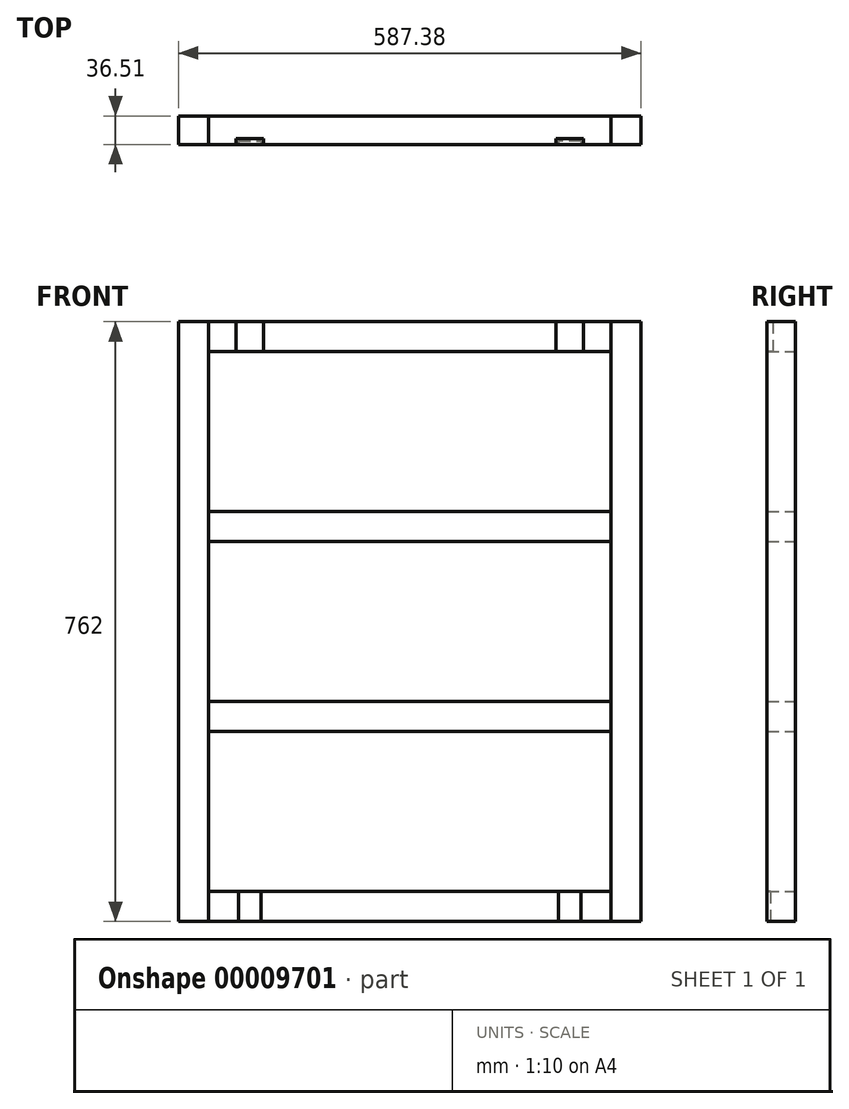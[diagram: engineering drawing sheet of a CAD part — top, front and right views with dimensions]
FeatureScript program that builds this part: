
annotation { "Feature Type Name" : "Feature", "Feature Type Description" : "" }
export const myFeature = defineFeature(function(context is Context, id is Id, definition is map)
    precondition{}
    {
        {
            var Q0;
            Q0=qCreatedBy(makeId("Front.planeOp"),FACE);
            var sketch = newSketch(context, id + "F0", { "sketchPlane" : qUnion([Q0])});
            skLineSegment(sketch, "E0.rect.bottom", {"start": v(293.69, 381) * mm, "end": v(-293.69, 381) * mm});
            skLineSegment(sketch, "E0.rect.top", {"start": v(293.69, -381) * mm, "end": v(-293.69, -381) * mm});
            skLineSegment(sketch, "E0.rect.left", {"start": v(293.69, 381) * mm, "end": v(293.69, -381) * mm});
            skLineSegment(sketch, "E0.rect.right", {"start": v(-293.69, 381) * mm, "end": v(-293.69, -381) * mm});
            skPoint(sketch, "E0.rect.middle", {"position": v(0, 0) * mm});
            skLineSegment(sketch, "E1.0", {"start": v(255.59, 342.9) * mm, "end": v(-255.59, 342.9) * mm});
            skLineSegment(sketch, "E1.1", {"start": v(255.59, 342.9) * mm, "end": v(255.59, -342.9) * mm});
            skLineSegment(sketch, "E1.2", {"start": v(255.59, -342.9) * mm, "end": v(-255.59, -342.9) * mm});
            skLineSegment(sketch, "E1.3", {"start": v(-255.59, 342.9) * mm, "end": v(-255.59, -342.9) * mm});
            skLineSegment(sketch, "E2", {"start": v(-255.59, 342.9) * mm, "end": v(-255.59, 381) * mm});
            skLineSegment(sketch, "E3", {"start": v(255.59, 342.9) * mm, "end": v(255.59, 381) * mm});
            skLineSegment(sketch, "E4", {"start": v(-255.59, -342.9) * mm, "end": v(-255.59, -381) * mm});
            skLineSegment(sketch, "E5", {"start": v(255.59, -342.9) * mm, "end": v(255.59, -381) * mm});
            skLineSegment(sketch, "E6", {"start": v(-255.59, 139.7) * mm, "end": v(255.59, 139.7) * mm});
            skLineSegment(sketch, "E7", {"start": v(-255.59, 101.6) * mm, "end": v(255.59, 101.6) * mm});
            skLineSegment(sketch, "E8", {"start": v(-255.59, -101.6) * mm, "end": v(255.59, -101.6) * mm});
            skLineSegment(sketch, "E9", {"start": v(-255.59, -139.7) * mm, "end": v(255.59, -139.7) * mm});
            skLineSegment(sketch, "E10", {"start": v(0, 342.9) * mm, "end": v(0, 139.7) * mm, "construction": true});
            skLineSegment(sketch, "E11", {"start": v(0, 101.6) * mm, "end": v(0, -101.6) * mm, "construction": true});
            skLineSegment(sketch, "E12", {"start": v(0, -139.7) * mm, "end": v(0, -342.9) * mm, "construction": true});
            skLineSegment(sketch, "E13", {"start": v(0, 139.7) * mm, "end": v(0, 101.6) * mm, "construction": true});
            skLineSegment(sketch, "E14", {"start": v(0, -101.6) * mm, "end": v(0, -139.7) * mm, "construction": true});
            skSolve(sketch);
        }
        {
            var Q0;
            {var subQ7=sQuery(id+"F0.wireOp",EDGE,"E0.rect.right");Q0=makeQuery(id+"F0.imprint","IMPRINT",FACE,{"disambiguationData":[TD([[makeQuery(id+"F0.imprint","IMPRINT",EDGE,{"derivedFrom":subQ7}),1.0]])]});}
            var Q1;
            {var subQ7=sQuery(id+"F0.wireOp",EDGE,"E0.rect.left");Q1=makeQuery(id+"F0.imprint","IMPRINT",FACE,{"disambiguationData":[TD([[makeQuery(id+"F0.imprint","IMPRINT",EDGE,{"derivedFrom":subQ7}),-1.0]])]});}
            extrude(context, id + "F1", {"entities" : qUnion([Q0, Q1]), "depth" : 36.5 * mm});
        }
        {
            var Q0;
            Q0=makeQuery(id+"F0.imprint","IMPRINT",FACE,{"disambiguationData":[TD([[makeQuery(id+"F0.imprint","IMPRINT",EDGE,{"derivedFrom":sQuery(id+"F0.wireOp",EDGE,"E1.0")}),-1.0]])]});
            var Q1;
            {var subQ1=sQuery(id+"F0.wireOp",EDGE,"E6");Q1=makeQuery(id+"F0.imprint","IMPRINT",FACE,{"disambiguationData":[TD([[makeQuery(id+"F0.imprint","IMPRINT",EDGE,{"derivedFrom":subQ1}),-1.0]])]});}
            var Q2;
            {var subQ0=sQuery(id+"F0.wireOp",EDGE,"E8");Q2=makeQuery(id+"F0.imprint","IMPRINT",FACE,{"disambiguationData":[TD([[makeQuery(id+"F0.imprint","IMPRINT",EDGE,{"derivedFrom":subQ0}),-1.0]])]});}
            var Q3;
            Q3=makeQuery(id+"F0.imprint","IMPRINT",FACE,{"disambiguationData":[TD([[makeQuery(id+"F0.imprint","IMPRINT",EDGE,{"derivedFrom":sQuery(id+"F0.wireOp",EDGE,"E1.2")}),1.0]])]});
            var Q4;
            Q4=makeQuery(id+"F1.opExtrude","CAP_FACE",FACE,{"disambiguationData":[OSD([sQuery(id+"F0.wireOp",EDGE,"E0.rect.bottom"),sQuery(id+"F0.wireOp",EDGE,"E0.rect.top"),sQuery(id+"F0.wireOp",EDGE,"E0.rect.right"),sQuery(id+"F0.wireOp",EDGE,"E1.3"),sQuery(id+"F0.wireOp",EDGE,"E2"),sQuery(id+"F0.wireOp",EDGE,"E4")])],"isStart":false});
            extrude(context, id + "F2", {"entities" : qUnion([Q0, Q1, Q2, Q3]), "endBound" : BoundingType.UP_TO_SURFACE, "endBoundEntityFace" : qUnion([Q4]), "depth" : 25.4 * mm});
        }
        {
            var Q0;
            {var subQ0=sQuery(id+"F0.wireOp",EDGE,"E2");var subQ1=sQuery(id+"F0.wireOp",EDGE,"E0.rect.bottom");Q0=makeQuery(id+"F2.opExtrude","CAP_FACE",FACE,{"disambiguationData":[OSD([subQ1,sQuery(id+"F0.wireOp",EDGE,"E0.rect.top"),sQuery(id+"F0.wireOp",EDGE,"E0.rect.right"),sQuery(id+"F0.wireOp",EDGE,"E1.3"),subQ0,sQuery(id+"F0.wireOp",EDGE,"E4")]),ownerDisambiguation([makeQuery(id+"F2.opExtrude","SWEPT_BODY",BODY,{"disambiguationData":[OSD([subQ1,sQuery(id+"F0.wireOp",EDGE,"E1.0"),subQ0,sQuery(id+"F0.wireOp",EDGE,"E3")])]})])],"isStart":false});}
            var sketch = newSketch(context, id + "F3", { "sketchPlane" : qUnion([Q0])});
            skLineSegment(sketch, "E15.bottom", {"start": v(-220.66, 381) * mm, "end": v(-185.74, 381) * mm});
            skLineSegment(sketch, "E15.top", {"start": v(-220.66, 342.9) * mm, "end": v(-185.74, 342.9) * mm});
            skLineSegment(sketch, "E15.left", {"start": v(-220.66, 381) * mm, "end": v(-220.66, 342.9) * mm});
            skLineSegment(sketch, "E15.right", {"start": v(-185.74, 381) * mm, "end": v(-185.74, 342.9) * mm});
            skLineSegment(sketch, "E16.bottom", {"start": v(-217.49, -342.9) * mm, "end": v(-188.91, -342.9) * mm});
            skLineSegment(sketch, "E16.top", {"start": v(-217.49, -381) * mm, "end": v(-188.91, -381) * mm});
            skLineSegment(sketch, "E16.left", {"start": v(-217.49, -342.9) * mm, "end": v(-217.49, -381) * mm});
            skLineSegment(sketch, "E16.right", {"start": v(-188.91, -342.9) * mm, "end": v(-188.91, -381) * mm});
            skLineSegment(sketch, "E17", {"start": v(-203.2, 342.9) * mm, "end": v(-203.2, -342.9) * mm, "construction": true});
            skLineSegment(sketch, "E18", {"start": v(0, 342.9) * mm, "end": v(0, -342.9) * mm, "construction": true});
            skLineSegment(sketch, "E19.MirrorCS", {"start": v(185.74, 381) * mm, "end": v(185.74, 342.9) * mm});
            skLineSegment(sketch, "E20.MirrorCS", {"start": v(220.66, 381) * mm, "end": v(220.66, 342.9) * mm});
            skLineSegment(sketch, "E21.MirrorCS", {"start": v(220.66, 342.9) * mm, "end": v(185.74, 342.9) * mm});
            skLineSegment(sketch, "E22.MirrorCS", {"start": v(220.66, 381) * mm, "end": v(185.74, 381) * mm});
            skLineSegment(sketch, "E23.MirrorCS", {"start": v(217.49, -342.9) * mm, "end": v(188.91, -342.9) * mm});
            skLineSegment(sketch, "E24.MirrorCS", {"start": v(188.91, -342.9) * mm, "end": v(188.91, -381) * mm});
            skLineSegment(sketch, "E25.MirrorCS", {"start": v(217.49, -381) * mm, "end": v(188.91, -381) * mm});
            skLineSegment(sketch, "E26.MirrorCS", {"start": v(217.49, -342.9) * mm, "end": v(217.49, -381) * mm});
            skSolve(sketch);
        }
        {
            var Q0;
            Q0=makeQuery(id+"F3.imprint","IMPRINT",FACE,{"disambiguationData":[TD([[makeQuery(id+"F3.imprint","IMPRINT",EDGE,{"derivedFrom":sQuery(id+"F3.wireOp",EDGE,"E15.bottom")}),1.0]])]});
            var Q1;
            Q1=makeQuery(id+"F3.imprint","IMPRINT",FACE,{"disambiguationData":[TD([[makeQuery(id+"F3.imprint","IMPRINT",EDGE,{"derivedFrom":sQuery(id+"F3.wireOp",EDGE,"E19.MirrorCS")}),1.0]])]});
            extrude(context, id + "F4", {"entities" : qUnion([Q0, Q1]), "operationType" : NewBodyOperationType.REMOVE, "oppositeDirection" : true, "depth" : 7.94 * mm});
        }
        {
            var Q0;
            Q0=makeQuery(id+"F3.imprint","IMPRINT",FACE,{"disambiguationData":[TD([[makeQuery(id+"F3.imprint","IMPRINT",EDGE,{"derivedFrom":sQuery(id+"F3.wireOp",EDGE,"E16.bottom")}),-1.0]])]});
            var Q1;
            Q1=makeQuery(id+"F3.imprint","IMPRINT",FACE,{"disambiguationData":[TD([[makeQuery(id+"F3.imprint","IMPRINT",EDGE,{"derivedFrom":sQuery(id+"F3.wireOp",EDGE,"E23.MirrorCS")}),1.0]])]});
            extrude(context, id + "F5", {"entities" : qUnion([Q0, Q1]), "operationType" : NewBodyOperationType.REMOVE, "oppositeDirection" : true, "depth" : 4.76 * mm});
        }
    });
